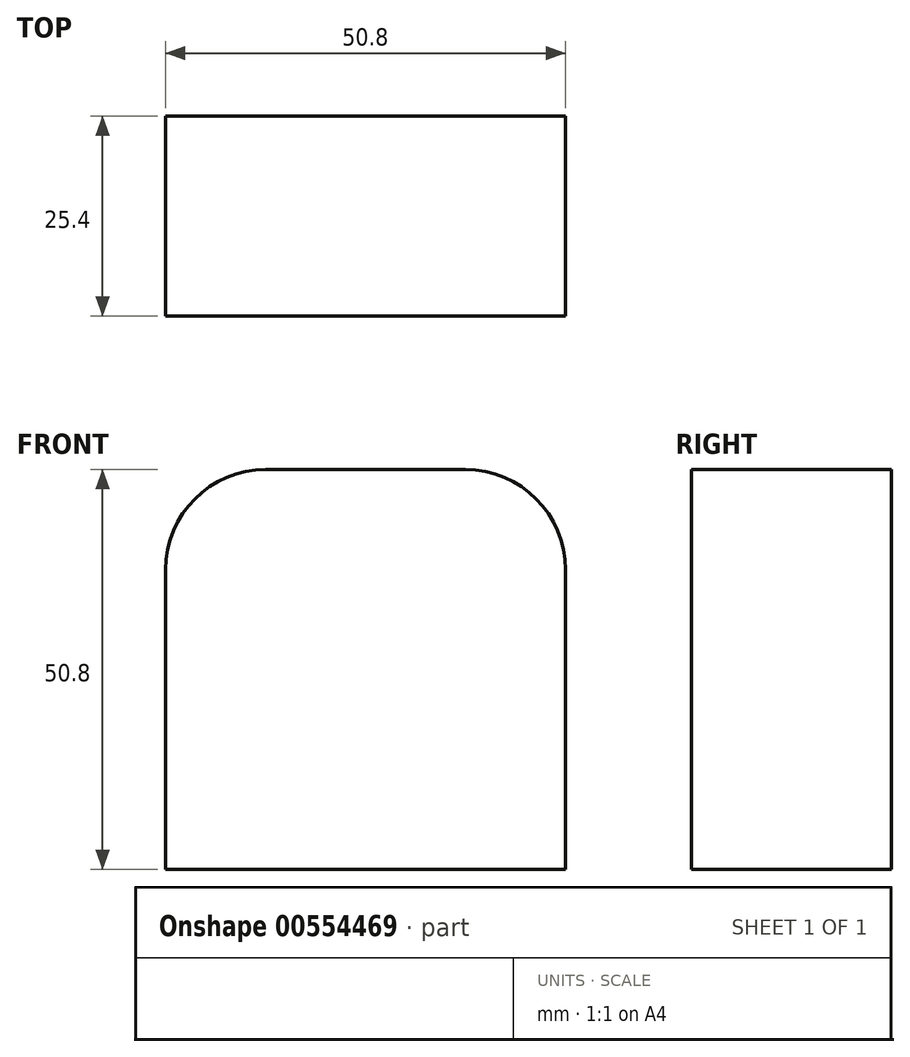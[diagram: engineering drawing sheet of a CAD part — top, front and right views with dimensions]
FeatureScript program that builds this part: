
annotation { "Feature Type Name" : "Feature", "Feature Type Description" : "" }
export const myFeature = defineFeature(function(context is Context, id is Id, definition is map)
    precondition{}
    {
        {
            var Q0;
            Q0=qCreatedBy(makeId("Front.planeOp"),FACE);
            var sketch = newSketch(context, id + "F0", { "sketchPlane" : qUnion([Q0])});
            skLineSegment(sketch, "E0.bottom", {"start": v(0, 0) * mm, "end": v(50.8, 0) * mm});
            skLineSegment(sketch, "E0.top", {"start": v(12.7, 50.8) * mm, "end": v(38.1, 50.8) * mm});
            skLineSegment(sketch, "E0.left", {"start": v(0, 0) * mm, "end": v(0, 38.1) * mm});
            skLineSegment(sketch, "E0.right", {"start": v(50.8, 0) * mm, "end": v(50.8, 38.1) * mm});
            skPoint(sketch, "E1.visualSharp", {"position": v(0, 50.8) * mm});
            skArc(sketch, "E1.filletArc", {"start": v(12.7, 50.8) * mm, "mid": v(3.72, 47.08) * mm, "end": v(0, 38.1) * mm});
            skPoint(sketch, "E2.visualSharp", {"position": v(50.8, 50.8) * mm});
            skArc(sketch, "E2.filletArc", {"start": v(50.8, 38.1) * mm, "mid": v(47.08, 47.08) * mm, "end": v(38.1, 50.8) * mm});
            skSolve(sketch);
        }
        {
            var Q0;
            Q0=makeQuery(id+"F0.imprint","IMPRINT",FACE,{"disambiguationData":[TD([[makeQuery(id+"F0.imprint","IMPRINT",EDGE,{"derivedFrom":sQuery(id+"F0.wireOp",EDGE,"E0.bottom")}),1.0]])]});
            extrude(context, id + "F1", {"entities" : qUnion([Q0]), "depth" : 25.4 * mm, "offsetDistance" : 25.4 * mm});
        }
        {
            var Q0;
            Q0=qCreatedBy(makeId("Front.planeOp"),FACE);
            var sketch = newSketch(context, id + "F2", { "sketchPlane" : qUnion([Q0])});
            skLineSegment(sketch, "E3", {"start": v(0, 0) * mm, "end": v(17.74, 0) * mm});
            skLineSegment(sketch, "E4", {"start": v(17.74, 0) * mm, "end": v(17.74, 7.72) * mm});
            skLineSegment(sketch, "E5", {"start": v(17.74, 7.72) * mm, "end": v(23.46, 7.72) * mm});
            skLineSegment(sketch, "E6", {"start": v(23.46, 7.72) * mm, "end": v(23.46, 12.5) * mm});
            skLineSegment(sketch, "E7", {"start": v(23.46, 12.5) * mm, "end": v(30.7, 12.5) * mm});
            skLineSegment(sketch, "E8", {"start": v(30.7, 12.5) * mm, "end": v(30.7, 7.72) * mm});
            skLineSegment(sketch, "E9", {"start": v(30.7, 7.72) * mm, "end": v(39.86, 7.72) * mm});
            skLineSegment(sketch, "E10", {"start": v(39.86, 7.72) * mm, "end": v(39.86, 0) * mm});
            skLineSegment(sketch, "E11", {"start": v(39.86, 0) * mm, "end": v(17.74, 0) * mm});
            skSolve(sketch);
        }
        {
            var Q0;
            Q0 = qSketchRegion(id + "F2", true);
            extrude(context, id + "F3", {"entities" : qUnion([Q0]), "operationType" : NewBodyOperationType.ADD, "depth" : 25.4 * mm, "offsetDistance" : 25.4 * mm});
        }
    });
